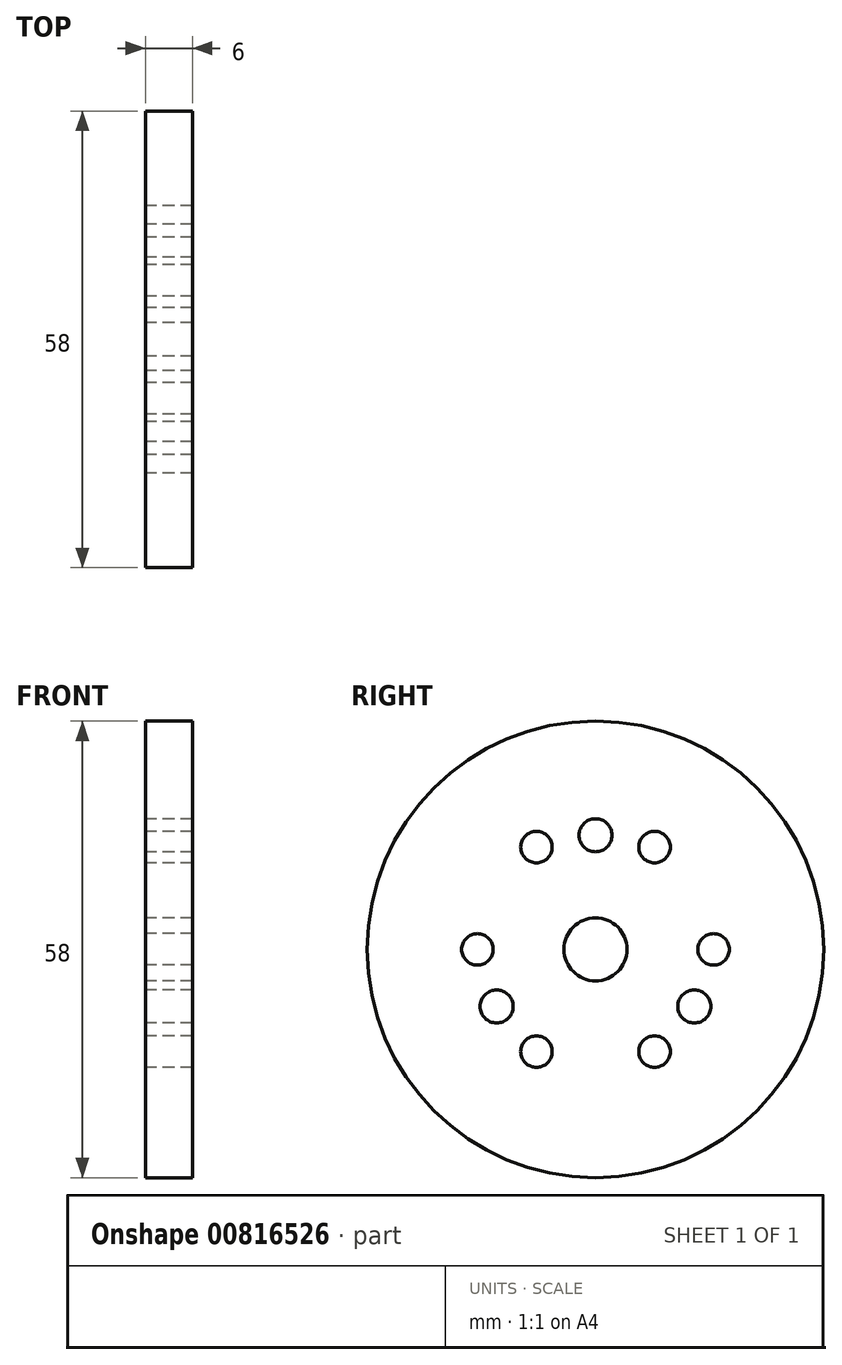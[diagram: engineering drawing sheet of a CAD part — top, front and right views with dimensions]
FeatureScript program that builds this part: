
annotation { "Feature Type Name" : "Feature", "Feature Type Description" : "" }
export const myFeature = defineFeature(function(context is Context, id is Id, definition is map)
    precondition{}
    {
        {
            var Q0;
            Q0=qCreatedBy(makeId("Right.planeOp"),FACE);
            var sketch = newSketch(context, id + "F0", { "sketchPlane" : qUnion([Q0])});
            skCircle(sketch, "E0", {"center": v(0, 0) * mm, "radius": 29 * mm});
            skCircle(sketch, "E1", {"center": v(0, 0) * mm, "radius": 14.5 * mm, "construction": true});
            skLineSegment(sketch, "E2", {"start": v(0, 65.04) * mm, "end": v(0, -65.63) * mm, "construction": true});
            skLineSegment(sketch, "E3", {"start": v(-69.13, 0) * mm, "end": v(64.07, 0) * mm, "construction": true});
            skLineSegment(sketch, "E4", {"start": v(0, 0) * mm, "end": v(56.85, -32.82) * mm, "construction": true});
            skLineSegment(sketch, "E5", {"start": v(0, 0) * mm, "end": v(29.3, -50.75) * mm, "construction": true});
            skLineSegment(sketch, "E6.MirrorCS", {"start": v(0, 0) * mm, "end": v(56.85, 32.82) * mm, "construction": true});
            skLineSegment(sketch, "E7.MirrorCS", {"start": v(0, 0) * mm, "end": v(29.3, 50.75) * mm, "construction": true});
            skLineSegment(sketch, "E8.MirrorCS", {"start": v(0, 0) * mm, "end": v(-29.3, 50.75) * mm, "construction": true});
            skLineSegment(sketch, "E9.MirrorCS", {"start": v(0, 0) * mm, "end": v(-56.85, 32.82) * mm, "construction": true});
            skLineSegment(sketch, "E10.MirrorCS", {"start": v(0, 0) * mm, "end": v(-56.85, -32.82) * mm, "construction": true});
            skLineSegment(sketch, "E11.MirrorCS", {"start": v(0, 0) * mm, "end": v(-29.3, -50.75) * mm, "construction": true});
            skCircle(sketch, "E12", {"center": v(0, 14.5) * mm, "radius": 2.1 * mm});
            skCircle(sketch, "E13", {"center": v(-12.56, -7.25) * mm, "radius": 2.1 * mm});
            skCircle(sketch, "E14", {"center": v(12.56, -7.25) * mm, "radius": 2.1 * mm});
            skCircle(sketch, "E15", {"center": v(0, 0) * mm, "radius": 15 * mm, "construction": true});
            skCircle(sketch, "E16", {"center": v(-7.5, -13) * mm, "radius": 2 * mm});
            skCircle(sketch, "E17", {"center": v(7.5, -13) * mm, "radius": 2 * mm});
            skCircle(sketch, "E18", {"center": v(15, 0) * mm, "radius": 2 * mm});
            skCircle(sketch, "E19", {"center": v(-15, 0) * mm, "radius": 2 * mm});
            skCircle(sketch, "E20", {"center": v(-7.5, 13) * mm, "radius": 2 * mm});
            skCircle(sketch, "E21", {"center": v(7.5, 13) * mm, "radius": 2 * mm});
            skCircle(sketch, "E22", {"center": v(0, 0) * mm, "radius": 4 * mm});
            skSolve(sketch);
        }
        {
            var Q0;
            Q0=qSketchRegion(id+"F0",true);
            extrude(context, id + "F1", {"entities" : qUnion([Q0]), "depth" : 6 * mm, "offsetDistance" : 25 * mm});
        }
    });
